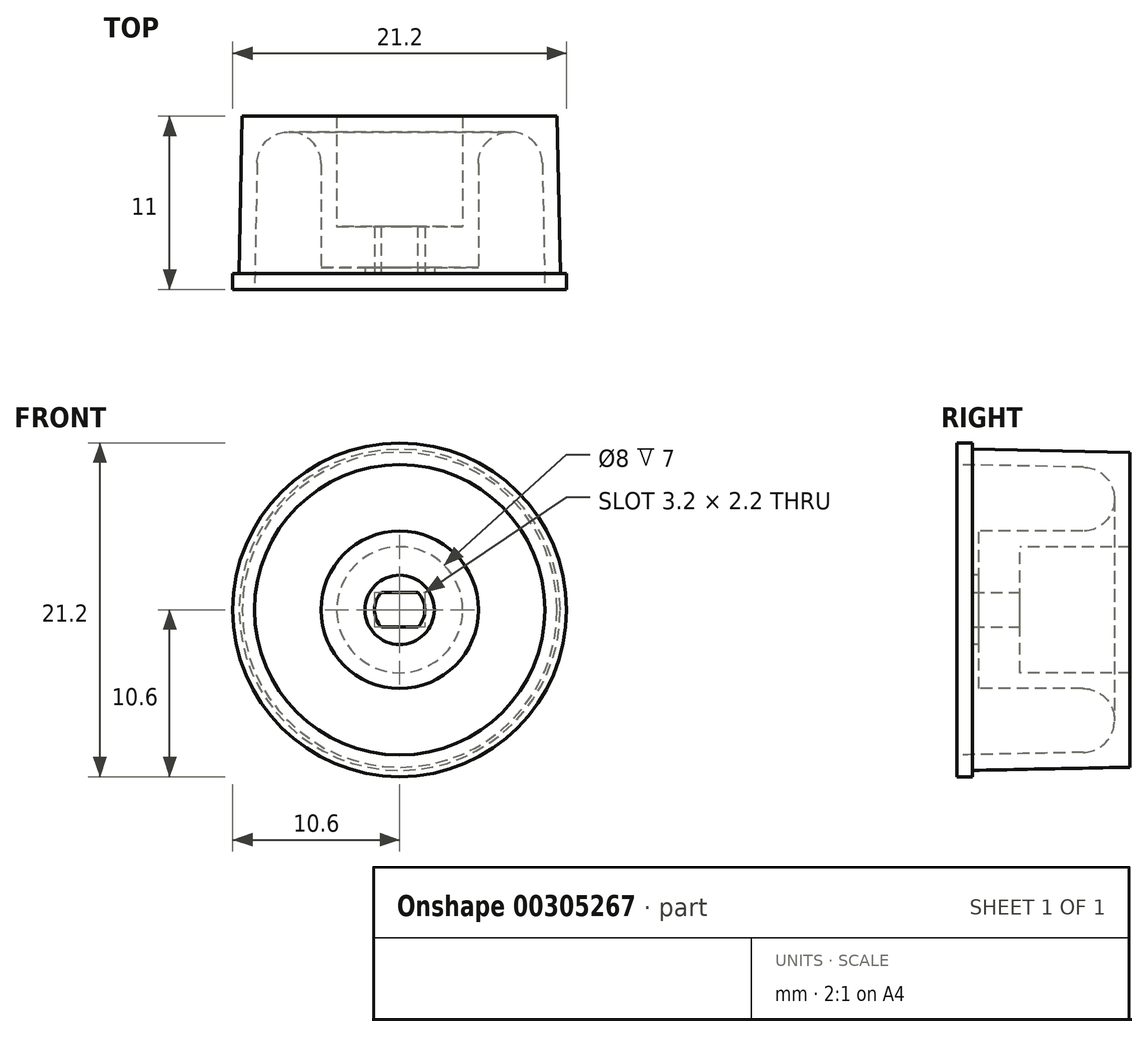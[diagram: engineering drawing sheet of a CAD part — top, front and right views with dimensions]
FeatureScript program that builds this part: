
annotation { "Feature Type Name" : "Feature", "Feature Type Description" : "" }
export const myFeature = defineFeature(function(context is Context, id is Id, definition is map)
    precondition{}
    {
        {
            var Q0;
            Q0=qCreatedBy(makeId("Right.planeOp"),FACE);
            var sketch = newSketch(context, id + "F0", { "sketchPlane" : qUnion([Q0])});
            skLineSegment(sketch, "E0", {"start": v(0, 0) * mm, "end": v(3, 0) * mm});
            skLineSegment(sketch, "E1", {"start": v(3, 0) * mm, "end": v(3, 2.4) * mm});
            skLineSegment(sketch, "E2", {"start": v(3, 2.4) * mm, "end": v(10, 2.4) * mm});
            skLineSegment(sketch, "E3", {"start": v(10, 2.4) * mm, "end": v(10, 8.4) * mm});
            skLineSegment(sketch, "E4", {"start": v(10, 8.4) * mm, "end": v(0, 8.6) * mm});
            skLineSegment(sketch, "E5", {"start": v(0, 8.6) * mm, "end": v(0, 9) * mm});
            skLineSegment(sketch, "E6", {"start": v(0, 9) * mm, "end": v(-1, 9) * mm});
            skLineSegment(sketch, "E7", {"start": v(-1, 9) * mm, "end": v(-1, 7.62) * mm});
            skLineSegment(sketch, "E8", {"start": v(-1, 7.62) * mm, "end": v(9, 7.42) * mm});
            skLineSegment(sketch, "E9", {"start": v(9, 7.42) * mm, "end": v(9, 3.4) * mm});
            skLineSegment(sketch, "E10", {"start": v(9, 3.4) * mm, "end": v(0.4, 3.4) * mm});
            skLineSegment(sketch, "E11", {"start": v(0.4, 3.4) * mm, "end": v(0.4, 0.6) * mm});
            skLineSegment(sketch, "E12", {"start": v(0.4, 0.6) * mm, "end": v(0, 0.6) * mm});
            skLineSegment(sketch, "E13", {"start": v(0, 0.6) * mm, "end": v(0, 0) * mm});
            skLineSegment(sketch, "E14", {"start": v(-4.93, -1.6) * mm, "end": v(16.57, -1.6) * mm, "construction": true});
            skSolve(sketch);
        }
        {
            var Q0;
            Q0=makeQuery(id+"F0.imprint","IMPRINT",FACE,{"disambiguationData":[TD([[makeQuery(id+"F0.imprint","IMPRINT",EDGE,{"derivedFrom":sQuery(id+"F0.wireOp",EDGE,"E0")}),1.0]])]});
            var Q1;
            Q1=sQuery(id+"F0.wireOp",EDGE,"E14");
            revolve(context, id + "F1", {"entities" : qUnion([Q0]), "axis" : qUnion([Q1]), "revolveType" : RevolveType.FULL});
        }
        {
            var Q0;
            Q0=makeQuery(id+"F1.opRevolve","SWEPT_FACE",FACE,{"disambiguationData":[OSD([sQuery(id+"F0.wireOp",EDGE,"E1")])]});
            var sketch = newSketch(context, id + "F2", { "sketchPlane" : qUnion([Q0])});
            skCircle(sketch, "E15", {"center": v(0, -1.6) * mm, "radius": 1.6 * mm});
            skLineSegment(sketch, "E16", {"start": v(-1.16, -0.5) * mm, "end": v(1.16, -0.5) * mm});
            skLineSegment(sketch, "E17", {"start": v(-1.16, -2.7) * mm, "end": v(1.16, -2.7) * mm});
            skSolve(sketch);
        }
        {
            var Q0;
            {var subQ0=sQuery(id+"F2.wireOp",EDGE,"E16");Q0=makeQuery(id+"F2.imprint","IMPRINT",FACE,{"disambiguationData":[TD([[makeQuery(id+"F2.imprint","IMPRINT",EDGE,{"derivedFrom":subQ0}),1.0]])]});}
            var Q1;
            {var subQ0=sQuery(id+"F2.wireOp",EDGE,"E17");Q1=makeQuery(id+"F2.imprint","IMPRINT",FACE,{"disambiguationData":[TD([[makeQuery(id+"F2.imprint","IMPRINT",EDGE,{"derivedFrom":subQ0}),-1.0]])]});}
            var Q2;
            Q2=makeQuery(id+"F1.opRevolve","SWEPT_FACE",FACE,{"disambiguationData":[OSD([sQuery(id+"F0.wireOp",EDGE,"E13")])]});
            extrude(context, id + "F3", {"entities" : qUnion([Q0, Q1]), "operationType" : NewBodyOperationType.ADD, "endBound" : BoundingType.UP_TO_SURFACE, "oppositeDirection" : true, "endBoundEntityFace" : qUnion([Q2]), "depth" : 25 * mm});
        }
        {
            var Q0;
            Q0=makeQuery(id+"F1.opRevolve","SWEPT_EDGE",EDGE,{"disambiguationData":[OSD([sQuery(id+"F0.wireOp",EDGE,"E8"),sQuery(id+"F0.wireOp",EDGE,"E9")])]});
            var Q1;
            Q1=makeQuery(id+"F1.opRevolve","SWEPT_EDGE",EDGE,{"disambiguationData":[OSD([sQuery(id+"F0.wireOp",EDGE,"E9"),sQuery(id+"F0.wireOp",EDGE,"E10")])]});
            fillet(context, id + "F4", {"entities" : qUnion([Q0, Q1]), "radius" : 2 * mm, "tangentPropagation" : true, "allowEdgeOverflow" : false});
        }
    });
